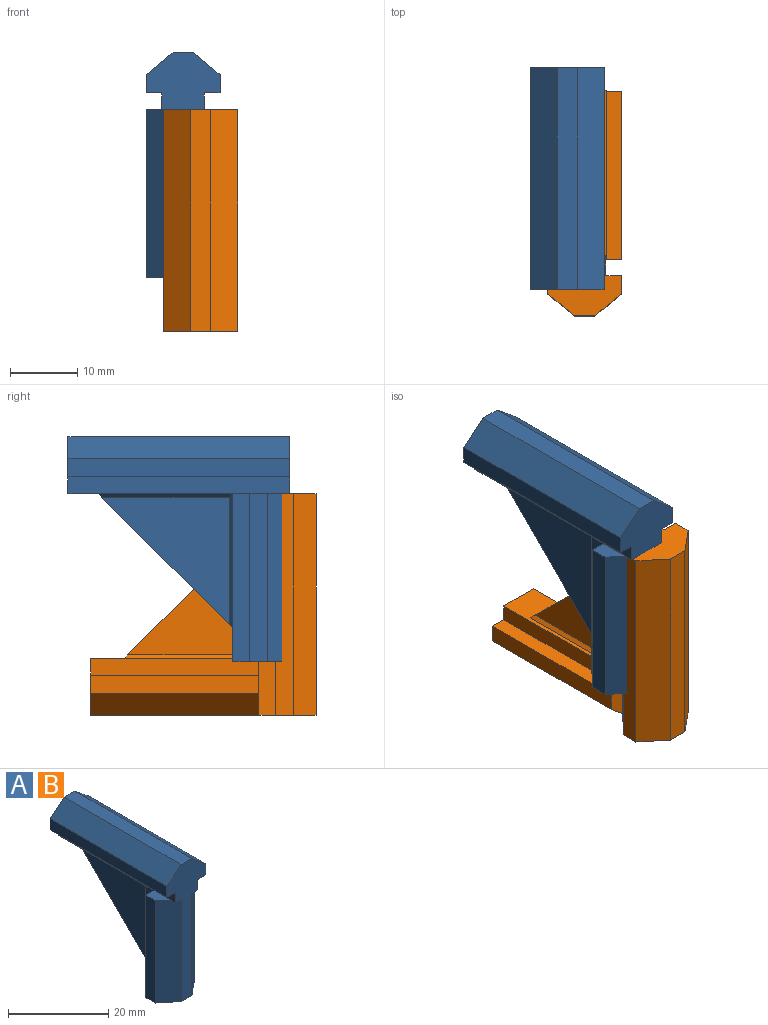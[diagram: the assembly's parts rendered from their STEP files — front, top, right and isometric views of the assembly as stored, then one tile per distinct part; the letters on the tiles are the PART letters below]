
ASSEMBLY  parts=2 mates=1
PART A: 35 faces, bbox 11x33x33.5 mm
  f0: plane 27x6.3mm, normal (0,0,-1), area 54.1mm2, adj f3,f11,f13,f15,f22,f23,f26,f29
  f1: plane 1.68x1.39mm, normal (0,0,-1), area 1.2mm2, adj f11,f12,f20
  f2: plane 1.62x1.33mm, normal (0,0,-1), area 1.1mm2, adj f3,f12,f19
  f3: plane 33x3mm, normal (1,0,0), area 82.6mm2, adj f0,f2,f4,f12,f13,f15,f25,f32
  f4: plane 33x2.35mm, normal (0,0,-1), area 77.5mm2, adj f3,f5,f12,f13
  f5: plane 33x2.7mm, normal (1,0,0), area 89.1mm2, adj f4,f6,f12,f13
  f6: plane 33x4mm, normal (0.64,0,0.77), area 171.1mm2, adj f5,f7,f12,f13
  f7: plane 33x3mm, normal (0,0,1), area 99mm2, adj f6,f8,f12,f13
  f8: plane 33x4mm, normal (-0.64,0,0.77), area 171.1mm2, adj f7,f9,f12,f13
  f9: plane 33x2.7mm, normal (-1,0,0), area 89.1mm2, adj f8,f10,f12,f13
  f10: plane 33x2.35mm, normal (0,0,-1), area 77.5mm2, adj f9,f11,f12,f13
  f11: plane 33x2.5mm, normal (-1,0,0), area 82.5mm2, adj f0,f1,f10,f12,f13,f14
  f12: plane 33.5x11mm, normal (0,-1,0), area 143.5mm2, adj f1,f2,f3,f4,f5,f6,f7,f8
  f13: plane 11x8.5mm, normal (0,1,0), area 68.5mm2, adj f0,f3,f4,f5,f6,f7,f8,f9
  f14: plane 4.61x2.32mm, normal (0,0,1), area 8.5mm2, adj f11,f20,f21,f22
  f15: plane 25x6.3mm, normal (0,1,0), area 57.2mm2, adj f0,f3,f16,f23,f24,f25,f26,f30
  f16: plane 25x2.5mm, normal (1,0,0), area 62.5mm2, adj f15,f17,f24,f25
  f17: plane 25x2.35mm, normal (0,1,0), area 58.7mm2, adj f16,f18,f24,f25
  f18: plane 25x2.7mm, normal (1,0,0), area 67.5mm2, adj f17,f19,f24,f25
  f19: plane 25x4mm, normal (0.64,-0.77,0), area 129.6mm2, adj f2,f12,f18,f24,f25
  f20: plane 25x4mm, normal (-0.64,-0.77,0), area 129.6mm2, adj f1,f12,f14,f21,f24
  f21: plane 25x2.7mm, normal (-1,0,0), area 67.5mm2, adj f14,f20,f22,f24
  f22: plane 25x2.35mm, normal (0,1,0), area 58.7mm2, adj f0,f14,f21,f23,f24
  f23: plane 25x2.5mm, normal (-1,0,0), area 62.5mm2, adj f0,f15,f22,f24
  f24: plane 11x8.5mm, normal (0,0,-1), area 68.5mm2, adj f12,f15,f16,f17,f18,f19,f20,f21
  f25: plane 7.17x2.38mm, normal (0,0,1), area 8.9mm2, adj f3,f15,f16,f17,f18,f19
  f26: plane 20x20mm, normal (0,0.71,-0.71), area 113.8mm2, adj f0,f15,f27,f28,f29,f30,f33,f34
  f27: plane 19x19mm, normal (1,0,0), area 180.5mm2, adj f26,f29,f30
  f28: plane 19x19mm, normal (-1,0,0), area 180.5mm2, adj f26,f33,f34
  f29: plane 19.5x0.5mm, normal (0.71,0,-0.71), area 13.6mm2, adj f0,f26,f27,f31
  f30: plane 19.5x0.5mm, normal (0.71,0.71,0), area 13.6mm2, adj f15,f26,f27,f31
  f31: plane 0.5x0.5mm, normal (0.58,0.58,-0.58), area 0.2mm2, adj f29,f30,f32
  f32: plane 0.65x0.5mm, normal (0,0.71,-0.71), area 0.5mm2, adj f0,f3,f15,f31
  f33: plane 20x0.5mm, normal (-0.71,0.71,0), area 13.8mm2, adj f15,f26,f28,f34
  f34: plane 20x0.5mm, normal (-0.71,0,-0.71), area 13.8mm2, adj f0,f26,f28,f33
PART B: same geometry as A
PLACE A t=(-18.23,5.95,-3.99)mm fixed
PLACE B rot(axis=(1,0,0),90deg) t=(-15.62,-23.7,-5.24)mm
MATE slider A.f2 <-> B.f13  axis (0,0,-1) through (-15.62,-26.61,-5.24)mm
